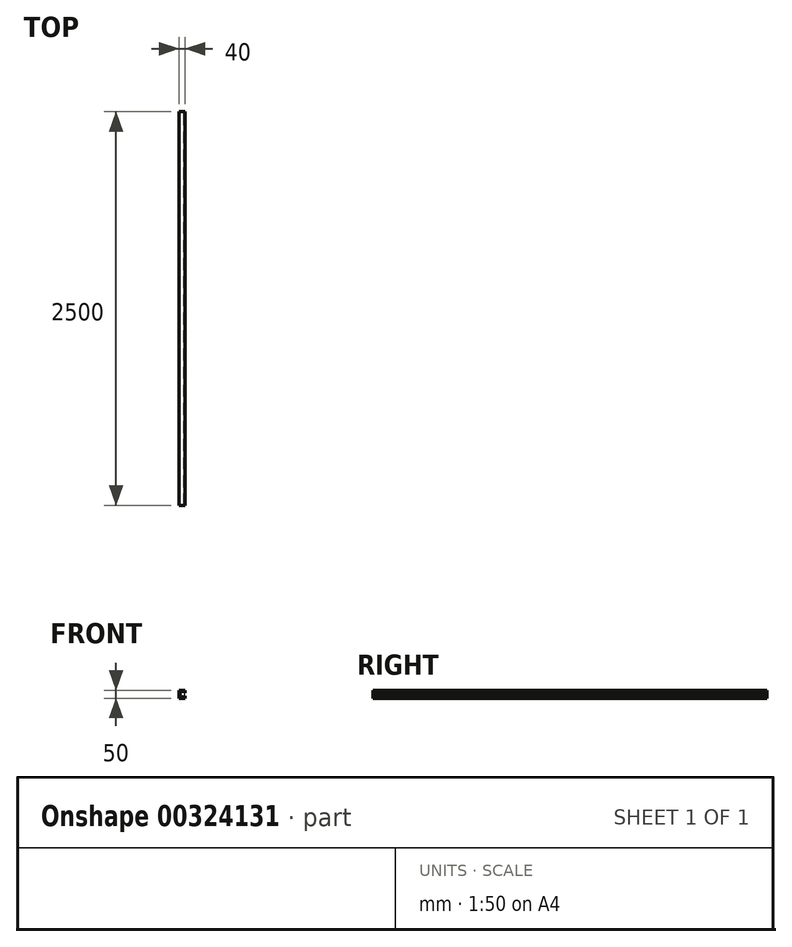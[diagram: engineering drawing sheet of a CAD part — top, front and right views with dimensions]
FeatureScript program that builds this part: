
annotation { "Feature Type Name" : "Feature", "Feature Type Description" : "" }
export const myFeature = defineFeature(function(context is Context, id is Id, definition is map)
    precondition{}
    {
        {
            var Q0;
            Q0=qCreatedBy(makeId("Front.planeOp"),FACE);
            var sketch = newSketch(context, id + "F0", { "sketchPlane" : qUnion([Q0])});
            skLineSegment(sketch, "E0.bottom", {"start": v(20, 25) * mm, "end": v(-20, 25) * mm});
            skLineSegment(sketch, "E0.top", {"start": v(20, -25) * mm, "end": v(-20, -25) * mm});
            skLineSegment(sketch, "E0.left", {"start": v(20, 25) * mm, "end": v(20, 10.07) * mm});
            skLineSegment(sketch, "E0.right", {"start": v(-20, 25) * mm, "end": v(-20, -25) * mm});
            skPoint(sketch, "E0.middle", {"position": v(0, 0) * mm});
            skLineSegment(sketch, "E1.bottom", {"start": v(12.5, 17.5) * mm, "end": v(-12.5, 17.5) * mm});
            skLineSegment(sketch, "E1.top", {"start": v(12.5, -17.5) * mm, "end": v(-12.5, -17.5) * mm});
            skLineSegment(sketch, "E1.left", {"start": v(12.5, 17.5) * mm, "end": v(12.5, 10.07) * mm});
            skLineSegment(sketch, "E1.right", {"start": v(-12.5, 17.5) * mm, "end": v(-12.5, -17.5) * mm});
            skLineSegment(sketch, "E2", {"start": v(20, 10.07) * mm, "end": v(12.5, 10.07) * mm});
            skLineSegment(sketch, "E3", {"start": v(20, -25) * mm, "end": v(20, -10.07) * mm});
            skLineSegment(sketch, "E4", {"start": v(20, -10.07) * mm, "end": v(12.5, -10.07) * mm});
            skLineSegment(sketch, "E5.trimOffspring", {"start": v(12.5, -10.07) * mm, "end": v(12.5, -17.5) * mm});
            skLineSegment(sketch, "E6.trimOffspring", {"start": v(20, -10.07) * mm, "end": v(20, -25) * mm});
            skSolve(sketch);
        }
        {
            var Q0;
            Q0=makeQuery(id+"F0.imprint","IMPRINT",FACE,{"disambiguationData":[TD([[makeQuery(id+"F0.imprint","IMPRINT",EDGE,{"derivedFrom":sQuery(id+"F0.wireOp",EDGE,"E0.bottom")}),1.0]])]});
            extrude(context, id + "F1", {"entities" : qUnion([Q0]), "depth" : 2500 * mm});
        }
    });
